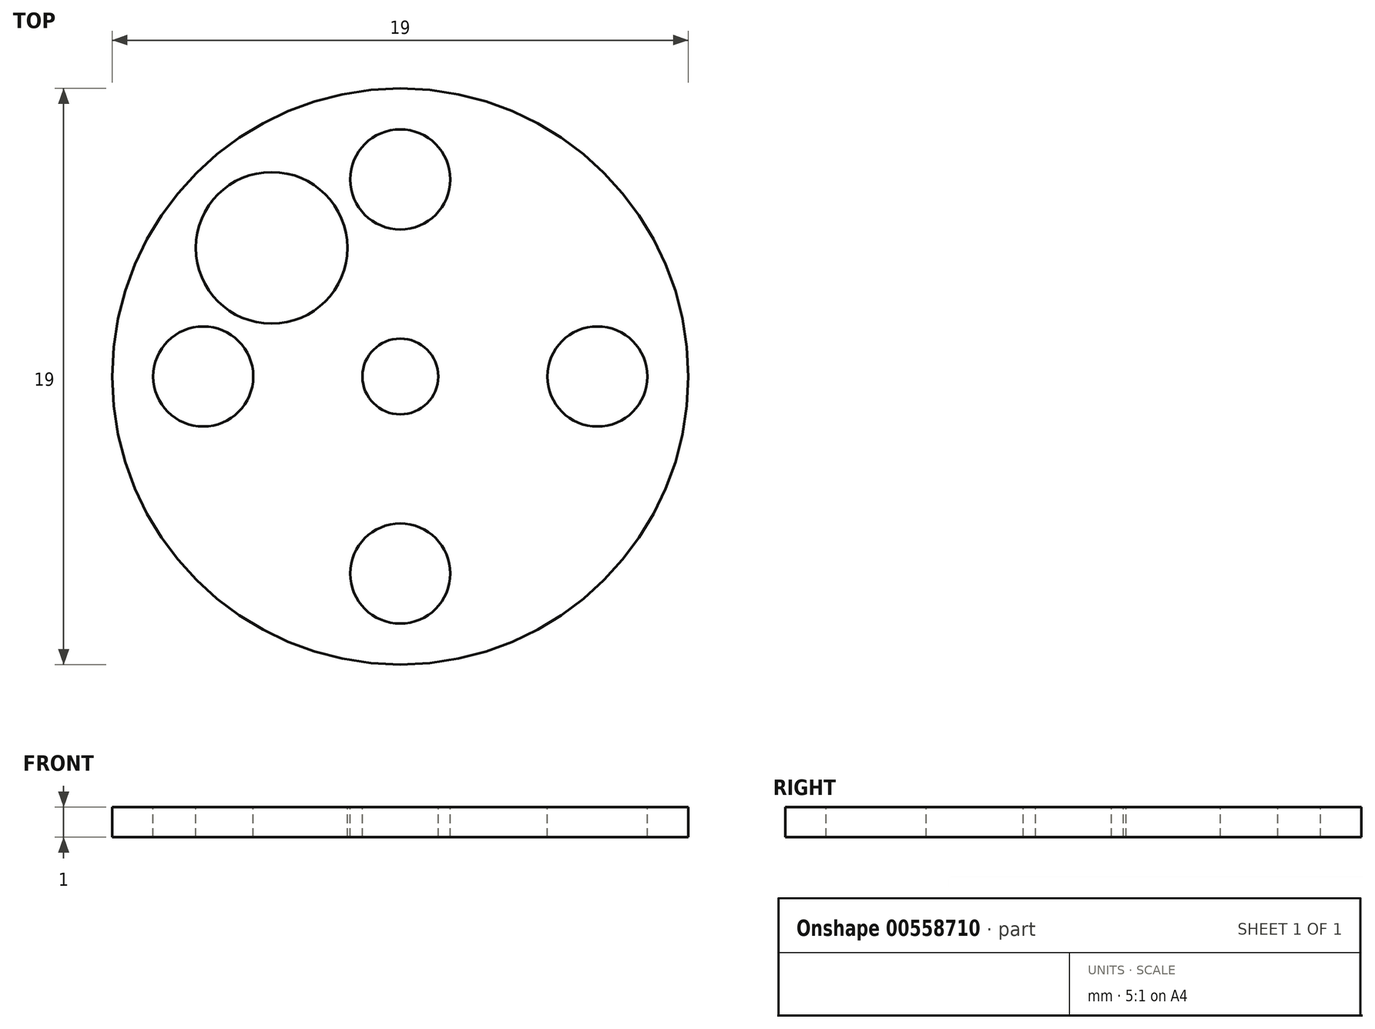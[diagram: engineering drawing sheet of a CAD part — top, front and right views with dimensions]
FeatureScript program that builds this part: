
annotation { "Feature Type Name" : "Feature", "Feature Type Description" : "" }
export const myFeature = defineFeature(function(context is Context, id is Id, definition is map)
    precondition{}
    {
        {
            var Q0;
            Q0=qCreatedBy(makeId("Top.planeOp"),FACE);
            var sketch = newSketch(context, id + "F0", { "sketchPlane" : qUnion([Q0])});
            skCircle(sketch, "E0", {"center": v(0, 0) * mm, "radius": 9.5 * mm});
            skCircle(sketch, "E1", {"center": v(0, 0) * mm, "radius": 6.5 * mm, "construction": true});
            skPoint(sketch, "E2", {"position": v(-6.5, 0) * mm});
            skPoint(sketch, "E3", {"position": v(6.5, 0) * mm});
            skPoint(sketch, "E4", {"position": v(0, -6.5) * mm});
            skPoint(sketch, "E5", {"position": v(0, 6.5) * mm});
            skLineSegment(sketch, "E6", {"start": v(0, 0) * mm, "end": v(-4.6, 4.6) * mm, "construction": true});
            skCircle(sketch, "E7", {"center": v(0, 0) * mm, "radius": 6 * mm, "construction": true});
            skPoint(sketch, "E8", {"position": v(-4.24, 4.24) * mm});
            skCircle(sketch, "E9", {"center": v(6.5, 0) * mm, "radius": 2.75 * mm, "construction": true});
            skSolve(sketch);
        }
        {
            var Q0;
            Q0=makeQuery(id+"F0.imprint","IMPRINT",FACE,{"disambiguationData":[TD([[makeQuery(id+"F0.imprint","IMPRINT",EDGE,{"derivedFrom":sQuery(id+"F0.wireOp",EDGE,"E0")}),1.0]])]});
            extrude(context, id + "F1", {"entities" : qUnion([Q0]), "oppositeDirection" : true, "depth" : 1 * mm, "offsetDistance" : 25 * mm});
        }
        {
            var Q0;
            Q0=sQuery(id+"F0.wireOp",VERTEX,"E5");
            var Q1;
            Q1=sQuery(id+"F0.wireOp",VERTEX,"E2");
            var Q2;
            Q2=sQuery(id+"F0.wireOp",VERTEX,"E4");
            var Q3;
            Q3=sQuery(id+"F0.wireOp",VERTEX,"E3");
            var Q4;
            Q4=makeQuery(id+"F1.opExtrude","SWEPT_BODY",BODY,{"disambiguationData":[OSD([sQuery(id+"F0.wireOp",EDGE,"E0")])]});
            hole(context, id + "F2", {"style" : HoleStyle.SIMPLE, "endStyle" : HoleEndStyle.THROUGH, "standardTappedOrClearance" : lookupTablePath({ "standard" : "ISO", "fit" : "Normal", "size" : "M3", "type" : "Clearance" }), "standardBlindInLast" : lookupTablePath({ "fit" : "Standard", "standard" : "ISO", "size" : "M3", "type" : "Clearance" }), "holeDiameter" : 3.3 * mm, "majorDiameter" : 5 * mm, "isTappedThrough" : true, "tappedDepth" : 3.6 * mm, "tapClearance" : 3, "locations" : qUnion([Q0, Q1, Q2, Q3]), "scope" : qUnion([Q4])});
        }
        {
            var Q0;
            Q0=sQuery(id+"F0.wireOp",VERTEX,"E8");
            var Q1;
            Q1=makeQuery(id+"F1.opExtrude","SWEPT_BODY",BODY,{"disambiguationData":[OSD([sQuery(id+"F0.wireOp",EDGE,"E0")])]});
            hole(context, id + "F3", {"style" : HoleStyle.SIMPLE, "endStyle" : HoleEndStyle.THROUGH, "standardTappedOrClearance" : lookupTablePath({ "standard" : "ISO", "size" : "5", "type" : "Drilled" }), "standardBlindInLast" : lookupTablePath({ "standard" : "ISO", "size" : "5", "type" : "Drilled" }), "holeDiameter" : 5 * mm, "majorDiameter" : 5 * mm, "isTappedThrough" : true, "tappedDepth" : 3.6 * mm, "tapClearance" : 3, "locations" : qUnion([Q0]), "scope" : qUnion([Q1])});
        }
        {
            var Q0;
            Q0=sQuery(id+"F0.wireOp",VERTEX,"E7.center");
            var Q1;
            Q1=makeQuery(id+"F1.opExtrude","SWEPT_BODY",BODY,{"disambiguationData":[OSD([sQuery(id+"F0.wireOp",EDGE,"E0")])]});
            hole(context, id + "F4", {"style" : HoleStyle.SIMPLE, "endStyle" : HoleEndStyle.THROUGH, "standardTappedOrClearance" : lookupTablePath({ "standard" : "ISO", "engagement" : "75%", "pitch" : "0.5 mm", "size" : "M3", "type" : "Tapped" }), "standardBlindInLast" : lookupTablePath({ "standard" : "ISO", "engagement" : "75%", "pitch" : "0.5 mm", "size" : "M3", "type" : "Tapped" }), "holeDiameter" : 2.5 * mm, "majorDiameter" : 3 * mm, "showTappedDepth" : true, "isTappedThrough" : true, "tappedDepth" : 3.6 * mm, "tapClearance" : 3, "locations" : qUnion([Q0]), "scope" : qUnion([Q1])});
        }
    });
